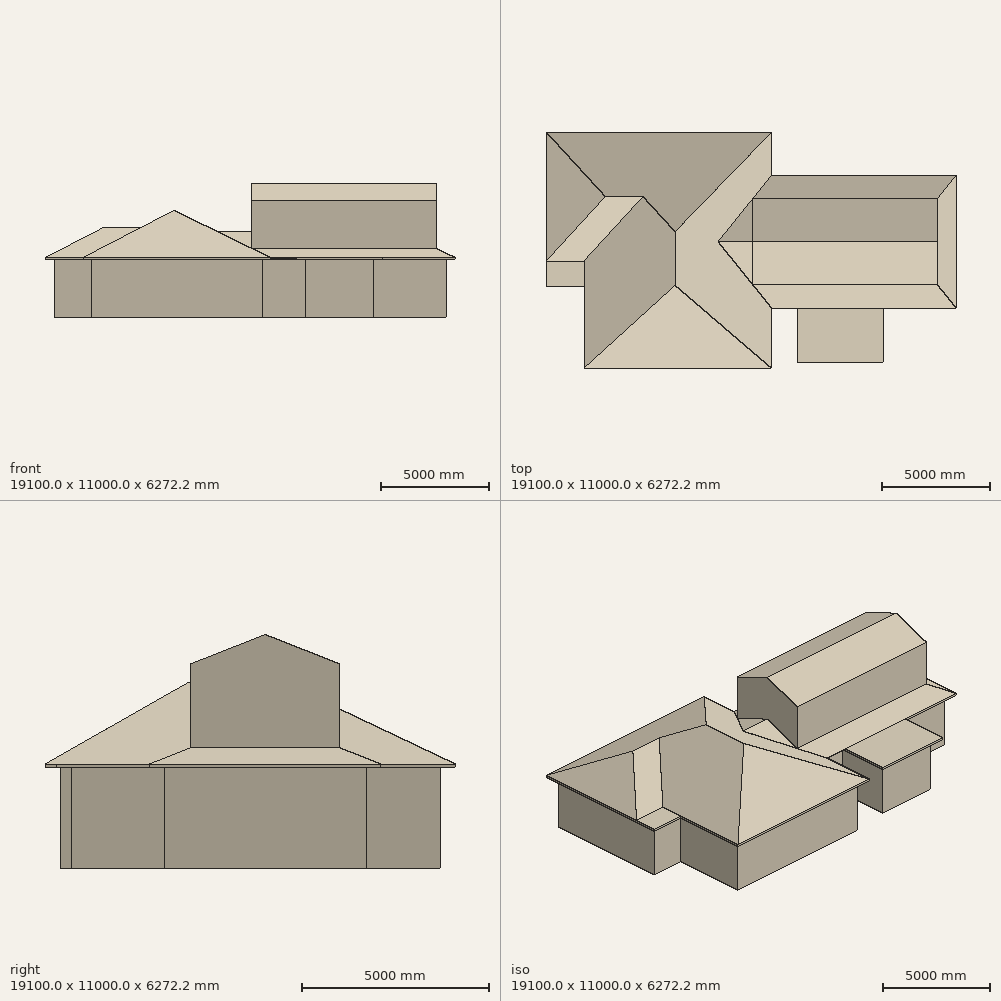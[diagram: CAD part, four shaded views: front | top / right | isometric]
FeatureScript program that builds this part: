
annotation { "Feature Type Name" : "Feature", "Feature Type Description" : "" }
export const myFeature = defineFeature(function(context is Context, id is Id, definition is map)
    precondition{}
    {
        {
            var Q0;
            Q0=qCreatedBy(makeId("Top.planeOp"),FACE);
            var sketch = newSketch(context, id + "F0", { "sketchPlane" : qUnion([Q0])});
            skLineSegment(sketch, "E0", {"start": v(0, 0) * mm, "end": v(10500, 0) * mm});
            skLineSegment(sketch, "E1", {"start": v(10500, 0) * mm, "end": v(10500, -2000) * mm});
            skLineSegment(sketch, "E2", {"start": v(10500, -2000) * mm, "end": v(19100, -2000) * mm});
            skLineSegment(sketch, "E3", {"start": v(19100, -2000) * mm, "end": v(19100, -8200) * mm});
            skLineSegment(sketch, "E4", {"start": v(19100, -8200) * mm, "end": v(15700, -8200) * mm});
            skLineSegment(sketch, "E5", {"start": v(15700, -8200) * mm, "end": v(15700, -10700) * mm});
            skLineSegment(sketch, "E6", {"start": v(15700, -10700) * mm, "end": v(11700, -10700) * mm});
            skLineSegment(sketch, "E7", {"start": v(11700, -10700) * mm, "end": v(11700, -8000) * mm});
            skLineSegment(sketch, "E8", {"start": v(11700, -8000) * mm, "end": v(10500, -8000) * mm});
            skLineSegment(sketch, "E9", {"start": v(10500, -8000) * mm, "end": v(10500, -11000) * mm});
            skLineSegment(sketch, "E10", {"start": v(10500, -11000) * mm, "end": v(1750, -11000) * mm});
            skLineSegment(sketch, "E11", {"start": v(0, -7200) * mm, "end": v(0, 0) * mm});
            skLineSegment(sketch, "E12", {"start": v(0, -7200) * mm, "end": v(1750, -7200) * mm});
            skLineSegment(sketch, "E13", {"start": v(1750, -7200) * mm, "end": v(1750, -11000) * mm});
            skLineSegment(sketch, "E14.0", {"start": v(400, -6800) * mm, "end": v(2150, -6800) * mm});
            skLineSegment(sketch, "E14.1", {"start": v(2150, -6800) * mm, "end": v(2150, -10600) * mm});
            skLineSegment(sketch, "E14.2", {"start": v(10100, -10600) * mm, "end": v(2150, -10600) * mm});
            skLineSegment(sketch, "E14.3", {"start": v(18700, -2400) * mm, "end": v(18700, -7800) * mm});
            skLineSegment(sketch, "E14.4", {"start": v(10100, -2400) * mm, "end": v(18700, -2400) * mm});
            skLineSegment(sketch, "E14.5", {"start": v(10100, -400) * mm, "end": v(10100, -2400) * mm});
            skLineSegment(sketch, "E14.6", {"start": v(400, -400) * mm, "end": v(10100, -400) * mm});
            skLineSegment(sketch, "E14.7", {"start": v(18700, -7800) * mm, "end": v(15300, -7800) * mm});
            skLineSegment(sketch, "E14.8", {"start": v(15300, -7800) * mm, "end": v(15300, -10300) * mm});
            skLineSegment(sketch, "E14.9", {"start": v(15300, -10300) * mm, "end": v(12100, -10300) * mm});
            skLineSegment(sketch, "E14.10", {"start": v(400, -6800) * mm, "end": v(400, -400) * mm});
            skLineSegment(sketch, "E14.11", {"start": v(12100, -10300) * mm, "end": v(12100, -7600) * mm});
            skLineSegment(sketch, "E14.12", {"start": v(12100, -7600) * mm, "end": v(10100, -7600) * mm});
            skLineSegment(sketch, "E14.13", {"start": v(10100, -7600) * mm, "end": v(10100, -10600) * mm});
            skLineSegment(sketch, "E15.0", {"start": v(500, -6700) * mm, "end": v(2250, -6700) * mm});
            skLineSegment(sketch, "E15.1", {"start": v(2250, -6700) * mm, "end": v(2250, -10500) * mm});
            skLineSegment(sketch, "E15.2", {"start": v(10000, -10500) * mm, "end": v(2250, -10500) * mm});
            skLineSegment(sketch, "E15.3", {"start": v(18600, -2500) * mm, "end": v(18600, -7700) * mm});
            skLineSegment(sketch, "E15.4", {"start": v(10000, -2500) * mm, "end": v(18600, -2500) * mm});
            skLineSegment(sketch, "E15.5", {"start": v(10000, -500) * mm, "end": v(10000, -2500) * mm});
            skLineSegment(sketch, "E15.6", {"start": v(500, -500) * mm, "end": v(10000, -500) * mm});
            skLineSegment(sketch, "E15.7", {"start": v(18600, -7700) * mm, "end": v(15200, -7700) * mm});
            skLineSegment(sketch, "E15.8", {"start": v(15200, -7700) * mm, "end": v(15200, -10200) * mm});
            skLineSegment(sketch, "E15.9", {"start": v(15200, -10200) * mm, "end": v(12200, -10200) * mm});
            skLineSegment(sketch, "E15.10", {"start": v(500, -6700) * mm, "end": v(500, -500) * mm});
            skLineSegment(sketch, "E15.11", {"start": v(12200, -10200) * mm, "end": v(12200, -7500) * mm});
            skLineSegment(sketch, "E15.12", {"start": v(12200, -7500) * mm, "end": v(10000, -7500) * mm});
            skLineSegment(sketch, "E15.13", {"start": v(10000, -7500) * mm, "end": v(10000, -10500) * mm});
            skSolve(sketch);
        }
        {
            var Q0;
            Q0=makeQuery(id+"F0.imprint","IMPRINT",FACE,{"disambiguationData":[TD([[makeQuery(id+"F0.imprint","IMPRINT",EDGE,{"derivedFrom":sQuery(id+"F0.wireOp",EDGE,"E14.0")}),1.0]])]});
            extrude(context, id + "F1", {"entities" : qUnion([Q0]), "depth" : 2700 * mm, "offsetDistance" : 25 * mm});
        }
        {
            var Q0;
            Q0=makeQuery(id+"F1.opExtrude","CAP_FACE",FACE,{"disambiguationData":[OSD([sQuery(id+"F0.wireOp",EDGE,"E14.0"),sQuery(id+"F0.wireOp",EDGE,"E14.1"),sQuery(id+"F0.wireOp",EDGE,"E14.2"),sQuery(id+"F0.wireOp",EDGE,"E14.3"),sQuery(id+"F0.wireOp",EDGE,"E14.4"),sQuery(id+"F0.wireOp",EDGE,"E14.5"),sQuery(id+"F0.wireOp",EDGE,"E14.6"),sQuery(id+"F0.wireOp",EDGE,"E14.7"),sQuery(id+"F0.wireOp",EDGE,"E14.8"),sQuery(id+"F0.wireOp",EDGE,"E14.9"),sQuery(id+"F0.wireOp",EDGE,"E14.10"),sQuery(id+"F0.wireOp",EDGE,"E14.11"),sQuery(id+"F0.wireOp",EDGE,"E14.12"),sQuery(id+"F0.wireOp",EDGE,"E14.13"),sQuery(id+"F0.wireOp",EDGE,"E15.0"),sQuery(id+"F0.wireOp",EDGE,"E15.1"),sQuery(id+"F0.wireOp",EDGE,"E15.2"),sQuery(id+"F0.wireOp",EDGE,"E15.3"),sQuery(id+"F0.wireOp",EDGE,"E15.4"),sQuery(id+"F0.wireOp",EDGE,"E15.5"),sQuery(id+"F0.wireOp",EDGE,"E15.6"),sQuery(id+"F0.wireOp",EDGE,"E15.7"),sQuery(id+"F0.wireOp",EDGE,"E15.8"),sQuery(id+"F0.wireOp",EDGE,"E15.9"),sQuery(id+"F0.wireOp",EDGE,"E15.10"),sQuery(id+"F0.wireOp",EDGE,"E15.11"),sQuery(id+"F0.wireOp",EDGE,"E15.12"),sQuery(id+"F0.wireOp",EDGE,"E15.13")])],"isStart":false});
            var sketch = newSketch(context, id + "F2", { "sketchPlane" : qUnion([Q0])});
            skLineSegment(sketch, "E16.0", {"start": v(10500, -11000) * mm, "end": v(1750, -11000) * mm});
            skLineSegment(sketch, "E17.0", {"start": v(1750, -7200) * mm, "end": v(1750, -11000) * mm});
            skLineSegment(sketch, "E18.0", {"start": v(0, -7200) * mm, "end": v(1750, -7200) * mm});
            skLineSegment(sketch, "E19.0", {"start": v(0, -7200) * mm, "end": v(0, 0) * mm});
            skLineSegment(sketch, "E20.0", {"start": v(0, 0) * mm, "end": v(10500, 0) * mm});
            skLineSegment(sketch, "E21.0", {"start": v(10500, 0) * mm, "end": v(10500, -2000) * mm});
            skLineSegment(sketch, "E22.0", {"start": v(10500, -2000) * mm, "end": v(19100, -2000) * mm});
            skLineSegment(sketch, "E23.0", {"start": v(19100, -2000) * mm, "end": v(19100, -8200) * mm});
            skLineSegment(sketch, "E24.0", {"start": v(19100, -8200) * mm, "end": v(15700, -8200) * mm});
            skLineSegment(sketch, "E25.0", {"start": v(15700, -8200) * mm, "end": v(15700, -10700) * mm});
            skLineSegment(sketch, "E26.0", {"start": v(15700, -10700) * mm, "end": v(11700, -10700) * mm});
            skLineSegment(sketch, "E27.0", {"start": v(11700, -10700) * mm, "end": v(11700, -8000) * mm});
            skLineSegment(sketch, "E28.0", {"start": v(11700, -8000) * mm, "end": v(10500, -8000) * mm});
            skLineSegment(sketch, "E29.0", {"start": v(10500, -8000) * mm, "end": v(10500, -11000) * mm});
            skSolve(sketch);
        }
        {
            var Q0;
            Q0=makeQuery(id+"F2.imprint","IMPRINT",FACE,{"disambiguationData":[TD([[makeQuery(id+"F2.imprint","IMPRINT",EDGE,{"derivedFrom":makeQuery(id+"F1.opExtrude","CAP_EDGE",EDGE,{"disambiguationData":[OSD([sQuery(id+"F0.wireOp",EDGE,"E15.0")])],"isStart":false})}),1.0]])]});
            var Q1;
            Q1=makeQuery(id+"F2.imprint","IMPRINT",FACE,{"disambiguationData":[TD([[makeQuery(id+"F2.imprint","IMPRINT",EDGE,{"derivedFrom":makeQuery(id+"F1.opExtrude","CAP_EDGE",EDGE,{"disambiguationData":[OSD([sQuery(id+"F0.wireOp",EDGE,"E14.0")])],"isStart":false})}),1.0]])]});
            var Q2;
            Q2=makeQuery(id+"F2.imprint","IMPRINT",FACE,{"disambiguationData":[TD([[makeQuery(id+"F2.imprint","IMPRINT",EDGE,{"derivedFrom":sQuery(id+"F2.wireOp",EDGE,"E16.0")}),-1.0]])]});
            extrude(context, id + "F3", {"entities" : qUnion([Q0, Q1, Q2]), "operationType" : NewBodyOperationType.ADD, "depth" : 100 * mm, "offsetDistance" : 25 * mm});
        }
        {
            var Q0;
            Q0=makeQuery(id+"F3.opExtrude","CAP_FACE",FACE,{"disambiguationData":[OSD([sQuery(id+"F2.wireOp",EDGE,"E16.0"),sQuery(id+"F2.wireOp",EDGE,"E17.0"),sQuery(id+"F2.wireOp",EDGE,"E18.0"),sQuery(id+"F2.wireOp",EDGE,"E19.0"),sQuery(id+"F2.wireOp",EDGE,"E20.0"),sQuery(id+"F2.wireOp",EDGE,"E21.0"),sQuery(id+"F2.wireOp",EDGE,"E22.0"),sQuery(id+"F2.wireOp",EDGE,"E23.0"),sQuery(id+"F2.wireOp",EDGE,"E24.0"),sQuery(id+"F2.wireOp",EDGE,"E25.0"),sQuery(id+"F2.wireOp",EDGE,"E26.0"),sQuery(id+"F2.wireOp",EDGE,"E27.0"),sQuery(id+"F2.wireOp",EDGE,"E28.0"),sQuery(id+"F2.wireOp",EDGE,"E29.0")])],"isStart":false});
            var sketch = newSketch(context, id + "F4", { "sketchPlane" : qUnion([Q0])});
            skLineSegment(sketch, "E30", {"start": v(6000, -4636.36) * mm, "end": v(6000, -7136.36) * mm});
            skLineSegment(sketch, "E31", {"start": v(0, -6000) * mm, "end": v(1750, -6000) * mm});
            skLineSegment(sketch, "E32", {"start": v(1750, -6000) * mm, "end": v(1750, -7200) * mm});
            skLineSegment(sketch, "E33", {"start": v(0, 0) * mm, "end": v(0, -6000) * mm});
            skLineSegment(sketch, "E34", {"start": v(0, -3000) * mm, "end": v(2750, -3000) * mm, "construction": true});
            skLineSegment(sketch, "E35", {"start": v(0, 0) * mm, "end": v(2750, -3000) * mm});
            skLineSegment(sketch, "E36", {"start": v(0, -6000) * mm, "end": v(2750, -3000) * mm});
            skLineSegment(sketch, "E37", {"start": v(1750, -6000) * mm, "end": v(4500, -3000) * mm});
            skLineSegment(sketch, "E38", {"start": v(2750, -3000) * mm, "end": v(4500, -3000) * mm});
            skLineSegment(sketch, "E39", {"start": v(4500, -3000) * mm, "end": v(6000, -4636.36) * mm});
            skLineSegment(sketch, "E40", {"start": v(1750, -6000) * mm, "end": v(1750, 0) * mm, "construction": true});
            skLineSegment(sketch, "E41", {"start": v(1750, 0) * mm, "end": v(6000, -4636.36) * mm, "construction": true});
            skLineSegment(sketch, "E42", {"start": v(6000, -4636.36) * mm, "end": v(10500, 0) * mm});
            skLineSegment(sketch, "E43", {"start": v(1750, -11000) * mm, "end": v(6000, -7136.36) * mm});
            skLineSegment(sketch, "E44", {"start": v(10500, -11000) * mm, "end": v(6000, -7136.36) * mm});
            skLineSegment(sketch, "E45", {"start": v(19100, -5100) * mm, "end": v(16600, -5100) * mm, "construction": true});
            skLineSegment(sketch, "E46", {"start": v(19100, -2000) * mm, "end": v(16600, -5100) * mm});
            skLineSegment(sketch, "E47", {"start": v(19100, -8200) * mm, "end": v(16600, -5100) * mm});
            skLineSegment(sketch, "E48", {"start": v(10500, -2000) * mm, "end": v(8000, -5100) * mm});
            skLineSegment(sketch, "E49", {"start": v(8000, -5100) * mm, "end": v(10500, -8000) * mm});
            skLineSegment(sketch, "E50", {"start": v(8000, -5100) * mm, "end": v(16600, -5100) * mm});
            skSolve(sketch);
        }
        {
            var Q0;
            Q0=qCreatedBy(makeId("Right.planeOp"),FACE);
            var Q1;
            Q1=sQuery(id+"F4.wireOp",EDGE,"E30");
            cPlane(context, id + "F5", {"entities" : qUnion([Q0, Q1]), "cplaneType" : CPlaneType.LINE_ANGLE, "offset" : 25 * mm, "angle" : 0 * degree, "width" : 150 * mm, "height" : 150 * mm});
        }
        {
            var Q0;
            Q0=qCreatedBy(id+"F5.planeOp",FACE);
            var sketch = newSketch(context, id + "F6", { "sketchPlane" : qUnion([Q0])});
            skPoint(sketch, "E51.0", {"position": v(4636.36, 2800) * mm});
            skPoint(sketch, "E52.0", {"position": v(7136.36, 2800) * mm});
            skLineSegment(sketch, "E53", {"start": v(7136.36, 2800) * mm, "end": v(7136.36, 5000) * mm});
            skLineSegment(sketch, "E54", {"start": v(7136.36, 5000) * mm, "end": v(4636.36, 5000) * mm});
            skLineSegment(sketch, "E55", {"start": v(4636.36, 5000) * mm, "end": v(4636.36, 2800) * mm});
            skSolve(sketch);
        }
        {
            var Q0;
            Q0=sQuery(id+"F6.wireOp",VERTEX,"E55.start");
            var Q1;
            Q1=sQuery(id+"F4.wireOp",VERTEX,"E42.end");
            var Q2;
            Q2=sQuery(id+"F4.wireOp",VERTEX,"E35.start");
            cPlane(context, id + "F7", {"entities" : qUnion([Q0, Q1, Q2]), "cplaneType" : CPlaneType.THREE_POINT, "offset" : 25 * mm, "width" : 150 * mm, "height" : 150 * mm});
        }
        {
            var Q0;
            Q0=qCreatedBy(makeId("Front.planeOp"),FACE);
            var Q1;
            Q1=sQuery(id+"F4.wireOp",EDGE,"E38");
            cPlane(context, id + "F8", {"entities" : qUnion([Q0, Q1]), "cplaneType" : CPlaneType.LINE_ANGLE, "offset" : 25 * mm, "angle" : 0 * degree, "width" : 150 * mm, "height" : 150 * mm});
        }
        {
            var Q0;
            Q0=qCreatedBy(id+"F8.planeOp",FACE);
            var sketch = newSketch(context, id + "F9", { "sketchPlane" : qUnion([Q0])});
            skPoint(sketch, "E56.0", {"position": v(-2750, 2800) * mm});
            skPoint(sketch, "E57.0", {"position": v(-4500, 2800) * mm});
            skLineSegment(sketch, "E58", {"start": v(-2750, 2800) * mm, "end": v(-2750, 5373.06) * mm});
            skLineSegment(sketch, "E59", {"start": v(-4500, 2800) * mm, "end": v(-4500, 5035.9) * mm});
            skSolve(sketch);
        }
        {
            var Q0;
            Q0=qCreatedBy(id+"F7.planeOp",FACE);
            var sketch = newSketch(context, id + "F10", { "sketchPlane" : qUnion([Q0])});
            skPoint(sketch, "E60.0", {"position": v(10500, 1200.35) * mm});
            skPoint(sketch, "E61.0", {"position": v(6000, 6332.2) * mm});
            skPoint(sketch, "E62.0", {"position": v(4500, 3910.7) * mm});
            skPoint(sketch, "E63.0", {"position": v(2750, 3910.7) * mm});
            skPoint(sketch, "E64.0", {"position": v(0, 1200.35) * mm});
            skLineSegment(sketch, "E65", {"start": v(10500, 1200.35) * mm, "end": v(6000, 6332.2) * mm});
            skLineSegment(sketch, "E66", {"start": v(10500, 1200.35) * mm, "end": v(0, 1200.35) * mm});
            skLineSegment(sketch, "E67.0", {"start": v(4500, 3910.7) * mm, "end": v(4500, 4869.22) * mm});
            skLineSegment(sketch, "E68.0", {"start": v(2750, 3910.7) * mm, "end": v(2750, 5013.75) * mm});
            skLineSegment(sketch, "E69", {"start": v(0, 1200.35) * mm, "end": v(2750, 4520.96) * mm});
            skLineSegment(sketch, "E70", {"start": v(2750, 4520.96) * mm, "end": v(4500, 4520.96) * mm});
            skLineSegment(sketch, "E71", {"start": v(4500, 4520.96) * mm, "end": v(6000, 6332.2) * mm});
            skSolve(sketch);
        }
        {
            var Q0;
            Q0=makeQuery(id+"F10.imprint","IMPRINT",FACE,{"disambiguationData":[TD([[makeQuery(id+"F10.imprint","IMPRINT",EDGE,{"derivedFrom":sQuery(id+"F10.wireOp",EDGE,"E65")}),1.0]])]});
            extrude(context, id + "F11", {"entities" : qUnion([Q0]), "operationType" : NewBodyOperationType.ADD, "depth" : 25 * mm, "offsetDistance" : 25 * mm});
        }
        {
            var Q0;
            Q0=sQuery(id+"F4.wireOp",VERTEX,"E43.start");
            var Q1;
            Q1=sQuery(id+"F6.wireOp",VERTEX,"E53.end");
            var Q2;
            Q2=sQuery(id+"F4.wireOp",VERTEX,"E44.start");
            cPlane(context, id + "F12", {"entities" : qUnion([Q0, Q1, Q2]), "cplaneType" : CPlaneType.THREE_POINT, "offset" : 25 * mm, "width" : 150 * mm, "height" : 150 * mm});
        }
        {
            var Q0;
            Q0=qCreatedBy(id+"F12.planeOp",FACE);
            var sketch = newSketch(context, id + "F13", { "sketchPlane" : qUnion([Q0])});
            skPoint(sketch, "E72.0", {"position": v(1750, -8173.48) * mm});
            skPoint(sketch, "E73.0", {"position": v(6000, -3727.4) * mm});
            skPoint(sketch, "E74.0", {"position": v(10500, -8173.48) * mm});
            skLineSegment(sketch, "E75", {"start": v(1750, -8173.48) * mm, "end": v(6000, -3727.4) * mm});
            skLineSegment(sketch, "E76", {"start": v(10500, -8173.48) * mm, "end": v(6000, -3727.4) * mm});
            skLineSegment(sketch, "E77", {"start": v(10500, -8173.48) * mm, "end": v(1750, -8173.48) * mm});
            skSolve(sketch);
        }
        {
            var Q0;
            Q0=makeQuery(id+"F13.imprint","IMPRINT",FACE,{"disambiguationData":[TD([[makeQuery(id+"F13.imprint","IMPRINT",EDGE,{"derivedFrom":sQuery(id+"F13.wireOp",EDGE,"E75")}),-1.0]])]});
            extrude(context, id + "F14", {"entities" : qUnion([Q0]), "oppositeDirection" : true, "depth" : 25 * mm, "offsetDistance" : 25 * mm});
        }
        {
            var Q0;
            Q0=sQuery(id+"F4.wireOp",VERTEX,"E35.start");
            var Q1;
            Q1=sQuery(id+"F4.wireOp",VERTEX,"E36.start");
            var Q2;
            Q2=makeQuery(id+"F11.opExtrude","CAP_VERTEX",VERTEX,{"disambiguationData":[OSD([sQuery(id+"F10.wireOp",EDGE,"E69"),sQuery(id+"F10.wireOp",EDGE,"E70")])],"isStart":true});
            cPlane(context, id + "F15", {"entities" : qUnion([Q0, Q1, Q2]), "cplaneType" : CPlaneType.THREE_POINT, "offset" : 25 * mm, "width" : 150 * mm, "height" : 150 * mm});
        }
        {
            var Q0;
            Q0=qCreatedBy(id+"F15.planeOp",FACE);
            var sketch = newSketch(context, id + "F16", { "sketchPlane" : qUnion([Q0])});
            skPoint(sketch, "E78.0", {"position": v(1287.18, 0) * mm});
            skPoint(sketch, "E79.0", {"position": v(1287.18, 6000) * mm});
            skPoint(sketch, "E80.0", {"position": v(4383.78, 3000) * mm});
            skLineSegment(sketch, "E81", {"start": v(1287.18, 0) * mm, "end": v(4383.78, 3000) * mm});
            skLineSegment(sketch, "E82", {"start": v(1287.18, 6000) * mm, "end": v(4383.78, 3000) * mm});
            skLineSegment(sketch, "E83", {"start": v(1287.18, 6000) * mm, "end": v(1287.18, 0) * mm});
            skSolve(sketch);
        }
        {
            var Q0;
            Q0=makeQuery(id+"F16.imprint","IMPRINT",FACE,{"disambiguationData":[TD([[makeQuery(id+"F16.imprint","IMPRINT",EDGE,{"derivedFrom":sQuery(id+"F16.wireOp",EDGE,"E81")}),1.0]])]});
            extrude(context, id + "F17", {"entities" : qUnion([Q0]), "operationType" : NewBodyOperationType.ADD, "depth" : 25 * mm, "offsetDistance" : 25 * mm});
        }
        {
            var Q0;
            Q0=sQuery(id+"F4.wireOp",VERTEX,"E36.start");
            var Q1;
            Q1=sQuery(id+"F4.wireOp",VERTEX,"E32.start");
            var Q2;
            Q2=makeQuery(id+"F11.opExtrude","CAP_VERTEX",VERTEX,{"disambiguationData":[OSD([sQuery(id+"F10.wireOp",EDGE,"E70"),sQuery(id+"F10.wireOp",EDGE,"E71")])],"isStart":true});
            cPlane(context, id + "F18", {"entities" : qUnion([Q0, Q1, Q2]), "cplaneType" : CPlaneType.THREE_POINT, "offset" : 25 * mm, "width" : 150 * mm, "height" : 150 * mm});
        }
        {
            var Q0;
            Q0=qCreatedBy(id+"F18.planeOp",FACE);
            var sketch = newSketch(context, id + "F19", { "sketchPlane" : qUnion([Q0])});
            skPoint(sketch, "E84.0", {"position": v(0, 4220.35) * mm});
            skPoint(sketch, "E85.0", {"position": v(1750, 4220.35) * mm});
            skLineSegment(sketch, "E86.0", {"start": v(2750, 899.74) * mm, "end": v(4500, 899.74) * mm});
            skLineSegment(sketch, "E87", {"start": v(4500, 899.74) * mm, "end": v(1750, 4220.35) * mm});
            skLineSegment(sketch, "E88", {"start": v(1750, 4220.35) * mm, "end": v(0, 4220.35) * mm});
            skLineSegment(sketch, "E89", {"start": v(0, 4220.35) * mm, "end": v(2750, 899.74) * mm});
            skSolve(sketch);
        }
        {
            var Q0;
            Q0=makeQuery(id+"F19.imprint","IMPRINT",FACE,{"disambiguationData":[TD([[makeQuery(id+"F19.imprint","IMPRINT",EDGE,{"derivedFrom":sQuery(id+"F19.wireOp",EDGE,"E86.0")}),1.0]])]});
            extrude(context, id + "F20", {"entities" : qUnion([Q0]), "operationType" : NewBodyOperationType.ADD, "depth" : 25 * mm, "offsetDistance" : 25 * mm});
        }
        {
            var Q0;
            Q0=sQuery(id+"F4.wireOp",VERTEX,"E43.start");
            var Q1;
            Q1=sQuery(id+"F6.wireOp",VERTEX,"E54.start");
            var Q2;
            Q2=sQuery(id+"F4.wireOp",VERTEX,"E32.start");
            cPlane(context, id + "F21", {"entities" : qUnion([Q0, Q1, Q2]), "cplaneType" : CPlaneType.THREE_POINT, "offset" : 25 * mm, "width" : 150 * mm, "height" : 150 * mm});
        }
        {
            var Q0;
            Q0=qCreatedBy(id+"F21.planeOp",FACE);
            var sketch = newSketch(context, id + "F22", { "sketchPlane" : qUnion([Q0])});
            skLineSegment(sketch, "E90.0", {"start": v(7626.96, 7136.36) * mm, "end": v(7626.96, 4636.36) * mm});
            skLineSegment(sketch, "E91.0", {"start": v(2841.3, 11000) * mm, "end": v(7626.96, 7136.36) * mm});
            skLineSegment(sketch, "E92.0", {"start": v(5937.9, 3000) * mm, "end": v(2841.3, 6000) * mm});
            skLineSegment(sketch, "E93.0", {"start": v(5937.9, 3000) * mm, "end": v(7626.96, 4636.36) * mm});
            skLineSegment(sketch, "E94.0", {"start": v(2841.3, 6000) * mm, "end": v(2841.3, 7200) * mm});
            skLineSegment(sketch, "E95.0", {"start": v(2841.3, 7200) * mm, "end": v(2841.3, 11000) * mm});
            skSolve(sketch);
        }
        {
            var Q0;
            Q0=makeQuery(id+"F22.imprint","IMPRINT",FACE,{"disambiguationData":[TD([[makeQuery(id+"F22.imprint","IMPRINT",EDGE,{"derivedFrom":sQuery(id+"F22.wireOp",EDGE,"E90.0")}),-1.0]])]});
            extrude(context, id + "F23", {"entities" : qUnion([Q0]), "depth" : 25 * mm, "offsetDistance" : 25 * mm});
        }
        {
            var Q0;
            Q0=sQuery(id+"F4.wireOp",VERTEX,"E44.start");
            var Q1;
            Q1=sQuery(id+"F4.wireOp",VERTEX,"E42.end");
            var Q2;
            Q2=sQuery(id+"F6.wireOp",VERTEX,"E55.start");
            cPlane(context, id + "F24", {"entities" : qUnion([Q0, Q1, Q2]), "cplaneType" : CPlaneType.THREE_POINT, "offset" : 25 * mm, "width" : 150 * mm, "height" : 150 * mm});
        }
        {
            var Q0;
            Q0=qCreatedBy(id+"F24.planeOp",FACE);
            var sketch = newSketch(context, id + "F25", { "sketchPlane" : qUnion([Q0])});
            skPoint(sketch, "E96.0", {"position": v(8203.25, 11000) * mm});
            skPoint(sketch, "E97.0", {"position": v(8203.25, 0) * mm});
            skPoint(sketch, "E98.0", {"position": v(3194.26, 4636.36) * mm});
            skPoint(sketch, "E99.0", {"position": v(3194.26, 7136.36) * mm});
            skLineSegment(sketch, "E100", {"start": v(8203.25, 11000) * mm, "end": v(3194.26, 7136.36) * mm});
            skLineSegment(sketch, "E101", {"start": v(3194.26, 7136.36) * mm, "end": v(3194.26, 4636.36) * mm});
            skLineSegment(sketch, "E102", {"start": v(3194.26, 4636.36) * mm, "end": v(8203.25, 0) * mm});
            skLineSegment(sketch, "E103", {"start": v(8203.25, 0) * mm, "end": v(8203.25, 11000) * mm});
            skSolve(sketch);
        }
        {
            var Q0;
            Q0=makeQuery(id+"F25.imprint","IMPRINT",FACE,{"disambiguationData":[TD([[makeQuery(id+"F25.imprint","IMPRINT",EDGE,{"derivedFrom":sQuery(id+"F25.wireOp",EDGE,"E100")}),1.0]])]});
            extrude(context, id + "F26", {"entities" : qUnion([Q0]), "depth" : 25 * mm, "offsetDistance" : 25 * mm});
        }
        {
            var Q0;
            Q0=sQuery(id+"F4.wireOp",EDGE,"E50");
            var Q1;
            Q1=qCreatedBy(makeId("Front.planeOp"),FACE);
            cPlane(context, id + "F27", {"entities" : qUnion([Q0, Q1]), "cplaneType" : CPlaneType.LINE_ANGLE, "offset" : 25 * mm, "angle" : 0 * degree, "width" : 150 * mm, "height" : 150 * mm});
        }
        {
            var Q0;
            Q0=qCreatedBy(id+"F27.planeOp",FACE);
            var sketch = newSketch(context, id + "F28", { "sketchPlane" : qUnion([Q0])});
            skPoint(sketch, "E104.0", {"position": v(-8000, 2800) * mm});
            skLineSegment(sketch, "E105.0.0", {"start": v(-10500, 2800) * mm, "end": v(-6000, 5000) * mm});
            skLineSegment(sketch, "E105.0.2", {"start": v(-6000, 5000) * mm, "end": v(-10500, 2800) * mm});
            skLineSegment(sketch, "E106", {"start": v(-8000, 2800) * mm, "end": v(-8000, 4022.22) * mm, "construction": true});
            skLineSegment(sketch, "E107", {"start": v(-8000, 4022.22) * mm, "end": v(-16600, 4022.22) * mm, "construction": true});
            skPoint(sketch, "E108.0", {"position": v(-16600, 2800) * mm});
            skLineSegment(sketch, "E109", {"start": v(-16600, 2800) * mm, "end": v(-16600, 4022.22) * mm});
            skSolve(sketch);
        }
        {
            var Q0;
            Q0=sQuery(id+"F4.wireOp",VERTEX,"E46.start");
            var Q1;
            Q1=sQuery(id+"F28.wireOp",VERTEX,"E107.end");
            var Q2;
            Q2=sQuery(id+"F28.wireOp",VERTEX,"E107.start");
            cPlane(context, id + "F29", {"entities" : qUnion([Q0, Q1, Q2]), "cplaneType" : CPlaneType.THREE_POINT, "offset" : 25 * mm, "width" : 150 * mm, "height" : 150 * mm});
        }
        {
            var Q0;
            Q0=qCreatedBy(id+"F29.planeOp",FACE);
            var sketch = newSketch(context, id + "F30", { "sketchPlane" : qUnion([Q0])});
            skPoint(sketch, "E110.0", {"position": v(19100, -2887.61) * mm});
            skLineSegment(sketch, "E111.0", {"start": v(10500, -2887.61) * mm, "end": v(19100, -2887.61) * mm});
            skPoint(sketch, "E112.0", {"position": v(16600, -6219.85) * mm});
            skPoint(sketch, "E113.0", {"position": v(8000, -6219.85) * mm});
            skLineSegment(sketch, "E114", {"start": v(19100, -2887.61) * mm, "end": v(16600, -6219.85) * mm});
            skLineSegment(sketch, "E115", {"start": v(16600, -6219.85) * mm, "end": v(8000, -6219.85) * mm});
            skLineSegment(sketch, "E116", {"start": v(8000, -6219.85) * mm, "end": v(10500, -2887.61) * mm});
            skSolve(sketch);
        }
        {
            var Q0;
            Q0=makeQuery(id+"F30.imprint","IMPRINT",FACE,{"disambiguationData":[TD([[makeQuery(id+"F30.imprint","IMPRINT",EDGE,{"derivedFrom":sQuery(id+"F30.wireOp",EDGE,"E111.0")}),-1.0]])]});
            extrude(context, id + "F31", {"entities" : qUnion([Q0]), "oppositeDirection" : true, "depth" : 25 * mm, "offsetDistance" : 25 * mm});
        }
        {
            var Q0;
            Q0=sQuery(id+"F28.wireOp",VERTEX,"E109.end");
            var Q1;
            Q1=sQuery(id+"F28.wireOp",VERTEX,"E107.start");
            var Q2;
            Q2=sQuery(id+"F4.wireOp",VERTEX,"E47.start");
            cPlane(context, id + "F32", {"entities" : qUnion([Q0, Q1, Q2]), "cplaneType" : CPlaneType.THREE_POINT, "offset" : 25 * mm, "width" : 150 * mm, "height" : 150 * mm});
        }
        {
            var Q0;
            Q0=qCreatedBy(id+"F32.planeOp",FACE);
            var sketch = newSketch(context, id + "F33", { "sketchPlane" : qUnion([Q0])});
            skPoint(sketch, "E117.0", {"position": v(8000, 3269.26) * mm});
            skPoint(sketch, "E118.0", {"position": v(16600, 3269.26) * mm});
            skPoint(sketch, "E119.0", {"position": v(19100, 6601.5) * mm});
            skLineSegment(sketch, "E120.0", {"start": v(10500, 6415.44) * mm, "end": v(10500, 9206.35) * mm});
            skLineSegment(sketch, "E121", {"start": v(8000, 3269.26) * mm, "end": v(16600, 3269.26) * mm});
            skLineSegment(sketch, "E122", {"start": v(16600, 3269.26) * mm, "end": v(19100, 6601.5) * mm});
            skLineSegment(sketch, "E123", {"start": v(19100, 6601.5) * mm, "end": v(10500, 6601.5) * mm});
            skLineSegment(sketch, "E124", {"start": v(10500, 6601.5) * mm, "end": v(8000, 3269.26) * mm});
            skSolve(sketch);
        }
        {
            var Q0;
            Q0=makeQuery(id+"F33.imprint","IMPRINT",FACE,{"disambiguationData":[TD([[makeQuery(id+"F33.imprint","IMPRINT",EDGE,{"derivedFrom":sQuery(id+"F33.wireOp",EDGE,"E121")}),1.0]])]});
            extrude(context, id + "F34", {"entities" : qUnion([Q0]), "depth" : 25 * mm, "offsetDistance" : 25 * mm});
        }
        {
            var Q0;
            Q0=sQuery(id+"F28.wireOp",VERTEX,"E109.end");
            var Q1;
            Q1=sQuery(id+"F4.wireOp",VERTEX,"E47.start");
            var Q2;
            Q2=sQuery(id+"F4.wireOp",VERTEX,"E46.start");
            cPlane(context, id + "F35", {"entities" : qUnion([Q0, Q1, Q2]), "cplaneType" : CPlaneType.THREE_POINT, "offset" : 25 * mm, "width" : 150 * mm, "height" : 150 * mm});
        }
        {
            var Q0;
            Q0=qCreatedBy(id+"F35.planeOp",FACE);
            var sketch = newSketch(context, id + "F36", { "sketchPlane" : qUnion([Q0])});
            skLineSegment(sketch, "E125.0", {"start": v(13146.58, 5100) * mm, "end": v(15929.35, 8200) * mm});
            skLineSegment(sketch, "E126.0", {"start": v(15929.35, 2000) * mm, "end": v(13146.58, 5100) * mm});
            skLineSegment(sketch, "E127.0", {"start": v(15929.35, 2000) * mm, "end": v(15929.35, 8200) * mm});
            skSolve(sketch);
        }
        {
            var Q0;
            Q0=makeQuery(id+"F36.imprint","IMPRINT",FACE,{"disambiguationData":[TD([[makeQuery(id+"F36.imprint","IMPRINT",EDGE,{"derivedFrom":sQuery(id+"F36.wireOp",EDGE,"E125.0")}),-1.0]])]});
            extrude(context, id + "F37", {"entities" : qUnion([Q0]), "depth" : 25 * mm, "offsetDistance" : 25 * mm});
        }
        {
            var Q0;
            Q0=makeQuery(id+"F37.opExtrude","CAP_FACE",FACE,{"disambiguationData":[OSD([sQuery(id+"F36.wireOp",EDGE,"E125.0"),sQuery(id+"F36.wireOp",EDGE,"E126.0"),sQuery(id+"F36.wireOp",EDGE,"E127.0")])],"isStart":true});
            var sketch = newSketch(context, id + "F38", { "sketchPlane" : qUnion([Q0])});
            skLineSegment(sketch, "E128", {"start": v(14941.92, -7100) * mm, "end": v(14941.92, -3100) * mm});
            skSolve(sketch);
        }
        {
            var Q0;
            Q0=sQuery(id+"F38.wireOp",EDGE,"E128");
            cPlane(context, id + "F39", {"entities" : qUnion([Q0]), "cplaneType" : CPlaneType.LINE_ANGLE, "offset" : 25 * mm, "angle" : 90 * degree, "width" : 150 * mm, "height" : 150 * mm});
        }
        {
            var Q0;
            Q0=qCreatedBy(id+"F39.planeOp",FACE);
            var sketch = newSketch(context, id + "F40", { "sketchPlane" : qUnion([Q0])});
            skLineSegment(sketch, "E129.0", {"start": v(-7100, 3233.7) * mm, "end": v(-3100, 3233.7) * mm});
            skLineSegment(sketch, "E130", {"start": v(-7100, 3233.7) * mm, "end": v(-7100, 5483.7) * mm});
            skLineSegment(sketch, "E131", {"start": v(-7100, 5483.7) * mm, "end": v(-5100, 6272.22) * mm});
            skLineSegment(sketch, "E132", {"start": v(-5100, 6272.22) * mm, "end": v(-3100, 5483.7) * mm});
            skLineSegment(sketch, "E133", {"start": v(-3100, 5483.7) * mm, "end": v(-3100, 3233.7) * mm});
            skLineSegment(sketch, "E134.0", {"start": v(-5100, 4022.22) * mm, "end": v(-8200, 2800) * mm, "construction": true});
            skLineSegment(sketch, "E135", {"start": v(-6592.73, 5683.7) * mm, "end": v(-3607.27, 5683.7) * mm, "construction": true});
            skSolve(sketch);
        }
        {
            var Q0;
            Q0=makeQuery(id+"F40.imprint","IMPRINT",FACE,{"disambiguationData":[TD([[makeQuery(id+"F40.imprint","IMPRINT",EDGE,{"derivedFrom":sQuery(id+"F40.wireOp",EDGE,"E129.0")}),1.0]])]});
            var Q1;
            Q1=makeQuery(id+"F26.opExtrude","CAP_FACE",FACE,{"disambiguationData":[OSD([sQuery(id+"F25.wireOp",EDGE,"E100"),sQuery(id+"F25.wireOp",EDGE,"E101"),sQuery(id+"F25.wireOp",EDGE,"E102"),sQuery(id+"F25.wireOp",EDGE,"E103")])],"isStart":true});
            var Q2;
            Q2=makeQuery(id+"F11.opExtrude","CAP_VERTEX",VERTEX,{"disambiguationData":[OSD([sQuery(id+"F10.wireOp",EDGE,"E65"),sQuery(id+"F10.wireOp",EDGE,"E71")])],"isStart":true});
            extrude(context, id + "F41", {"entities" : qUnion([Q0]), "oppositeDirection" : true, "depth" : 8600 * mm, "endBoundEntityFace" : qUnion([Q1]), "endBoundEntityVertex" : qUnion([Q2]), "offsetDistance" : 25 * mm});
        }
    });
